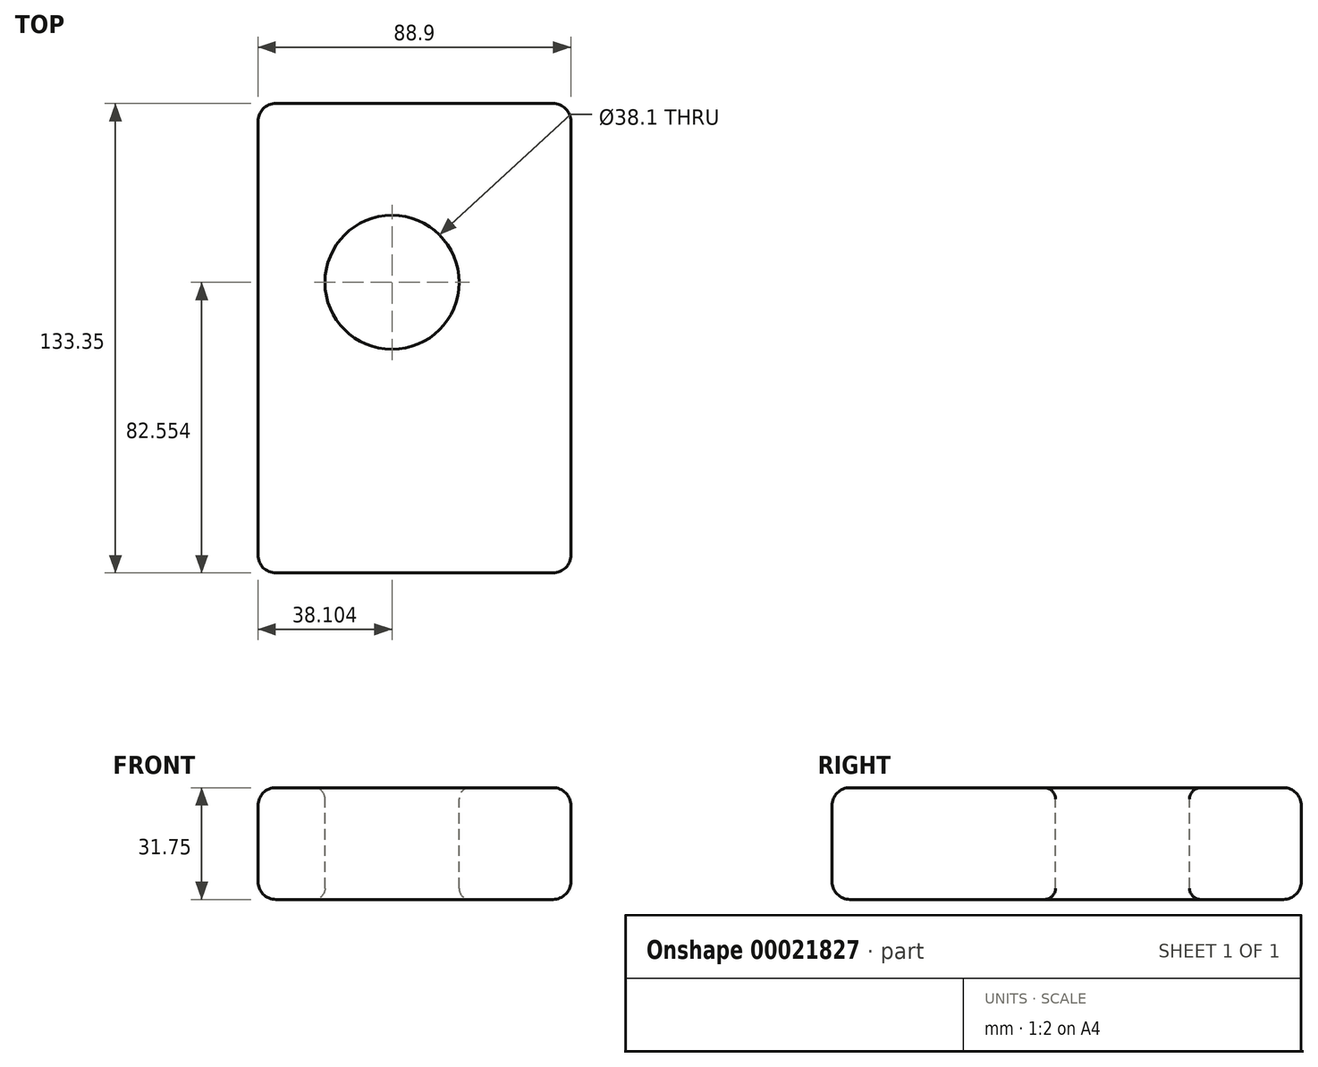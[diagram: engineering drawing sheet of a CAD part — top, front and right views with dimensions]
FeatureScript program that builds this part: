
annotation { "Feature Type Name" : "Feature", "Feature Type Description" : "" }
export const myFeature = defineFeature(function(context is Context, id is Id, definition is map)
    precondition{}
    {
        {
            var Q0;
            Q0=qCreatedBy(makeId("Top.planeOp"),FACE);
            var sketch = newSketch(context, id + "F0", { "sketchPlane" : qUnion([Q0])});
            skLineSegment(sketch, "E0.bottom", {"start": v(-73, -51) * mm, "end": v(15.9, -51) * mm});
            skLineSegment(sketch, "E0.top", {"start": v(-73, 82.34) * mm, "end": v(15.9, 82.34) * mm});
            skLineSegment(sketch, "E0.left", {"start": v(-73, -51) * mm, "end": v(-73, 82.34) * mm});
            skLineSegment(sketch, "E0.right", {"start": v(15.9, -51) * mm, "end": v(15.9, 82.34) * mm});
            skSolve(sketch);
        }
        {
            var Q0;
            Q0=makeQuery(id+"F0.imprint","IMPRINT",FACE,{"disambiguationData":[TD([[makeQuery(id+"F0.imprint","IMPRINT",EDGE,{"derivedFrom":sQuery(id+"F0.wireOp",EDGE,"E0.bottom")}),1.0]])]});
            extrude(context, id + "F1", {"entities" : qUnion([Q0]), "depth" : 31.75 * mm});
        }
        {
            var Q0;
            Q0=makeQuery(id+"F1.opExtrude","CAP_FACE",FACE,{"disambiguationData":[OSD([sQuery(id+"F0.wireOp",EDGE,"E0.bottom"),sQuery(id+"F0.wireOp",EDGE,"E0.top"),sQuery(id+"F0.wireOp",EDGE,"E0.left"),sQuery(id+"F0.wireOp",EDGE,"E0.right")])],"isStart":false});
            var Q1;
            Q1=makeQuery(id+"F1.opExtrude","CAP_FACE",FACE,{"disambiguationData":[OSD([sQuery(id+"F0.wireOp",EDGE,"E0.bottom"),sQuery(id+"F0.wireOp",EDGE,"E0.top"),sQuery(id+"F0.wireOp",EDGE,"E0.left"),sQuery(id+"F0.wireOp",EDGE,"E0.right")])],"isStart":true});
            var Q2;
            Q2=makeQuery(id+"F1.opExtrude","SWEPT_FACE",FACE,{"disambiguationData":[OSD([sQuery(id+"F0.wireOp",EDGE,"E0.right")])]});
            var Q3;
            Q3=makeQuery(id+"F1.opExtrude","SWEPT_FACE",FACE,{"disambiguationData":[OSD([sQuery(id+"F0.wireOp",EDGE,"E0.bottom")])]});
            var Q4;
            Q4=makeQuery(id+"F1.opExtrude","SWEPT_FACE",FACE,{"disambiguationData":[OSD([sQuery(id+"F0.wireOp",EDGE,"E0.left")])]});
            fillet(context, id + "F2", {"entities" : qUnion([Q0, Q1, Q2, Q3, Q4]), "radius" : 5.08 * mm, "tangentPropagation" : true, "allowEdgeOverflow" : false});
        }
        {
            var Q0;
            Q0=makeQuery(id+"F1.opExtrude","CAP_FACE",FACE,{"disambiguationData":[OSD([sQuery(id+"F0.wireOp",EDGE,"E0.bottom"),sQuery(id+"F0.wireOp",EDGE,"E0.top"),sQuery(id+"F0.wireOp",EDGE,"E0.left"),sQuery(id+"F0.wireOp",EDGE,"E0.right")])],"isStart":false});
            var sketch = newSketch(context, id + "F3", { "sketchPlane" : qUnion([Q0])});
            skCircle(sketch, "E1", {"center": v(-34.9, 31.54) * mm, "radius": 19.05 * mm});
            skSolve(sketch);
        }
        {
            var Q0;
            Q0 = qSketchRegion(id + "F3", true);
            extrude(context, id + "F4", {"entities" : qUnion([Q0]), "operationType" : NewBodyOperationType.REMOVE, "endBound" : BoundingType.THROUGH_ALL, "oppositeDirection" : true, "depth" : 25.4 * mm});
        }
        {
            var Q0;
            Q0=makeQuery(id+"F1.opExtrude","SWEPT_FACE",FACE,{"disambiguationData":[OSD([sQuery(id+"F0.wireOp",EDGE,"E0.right")])]});
            var Q1;
            Q1=makeQuery(id+"F4.boolean.opBoolean","COPY",FACE,{"derivedFrom":makeQuery(id+"F4.opExtrude","SWEPT_FACE",FACE,{"disambiguationData":[OSD([sQuery(id+"F3.wireOp",EDGE,"E1")])]})});
            fillet(context, id + "F5", {"entities" : qUnion([Q0, Q1]), "radius" : 3.17 * mm, "tangentPropagation" : true, "allowEdgeOverflow" : false});
        }
    });
